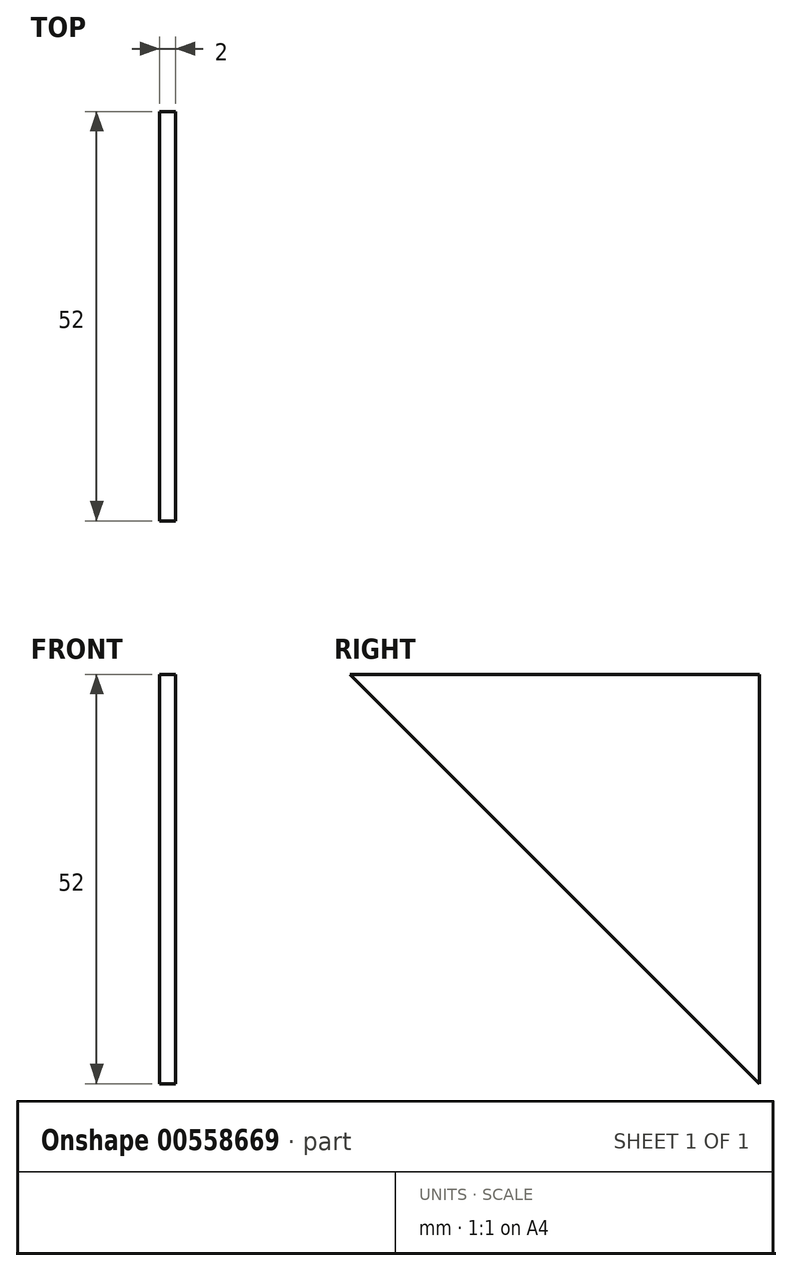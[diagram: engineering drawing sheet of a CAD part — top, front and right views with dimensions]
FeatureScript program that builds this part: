
annotation { "Feature Type Name" : "Feature", "Feature Type Description" : "" }
export const myFeature = defineFeature(function(context is Context, id is Id, definition is map)
    precondition{}
    {
        {
            var Q0;
            Q0=qCreatedBy(makeId("Right.planeOp"),FACE);
            var sketch = newSketch(context, id + "F0", { "sketchPlane" : qUnion([Q0])});
            skLineSegment(sketch, "E0", {"start": v(0, 0) * mm, "end": v(-52, 0) * mm});
            skLineSegment(sketch, "E1", {"start": v(0, 0) * mm, "end": v(0, -52) * mm});
            skLineSegment(sketch, "E2", {"start": v(0, -52) * mm, "end": v(-52, 0) * mm});
            skSolve(sketch);
        }
        {
            var Q0;
            Q0=makeQuery(id+"F0.imprint","IMPRINT",FACE,{"disambiguationData":[TD([[makeQuery(id+"F0.imprint","IMPRINT",EDGE,{"derivedFrom":sQuery(id+"F0.wireOp",EDGE,"E0")}),1.0]])]});
            extrude(context, id + "F1", {"entities" : qUnion([Q0]), "depth" : 2 * mm, "offsetDistance" : 25 * mm});
        }
    });
